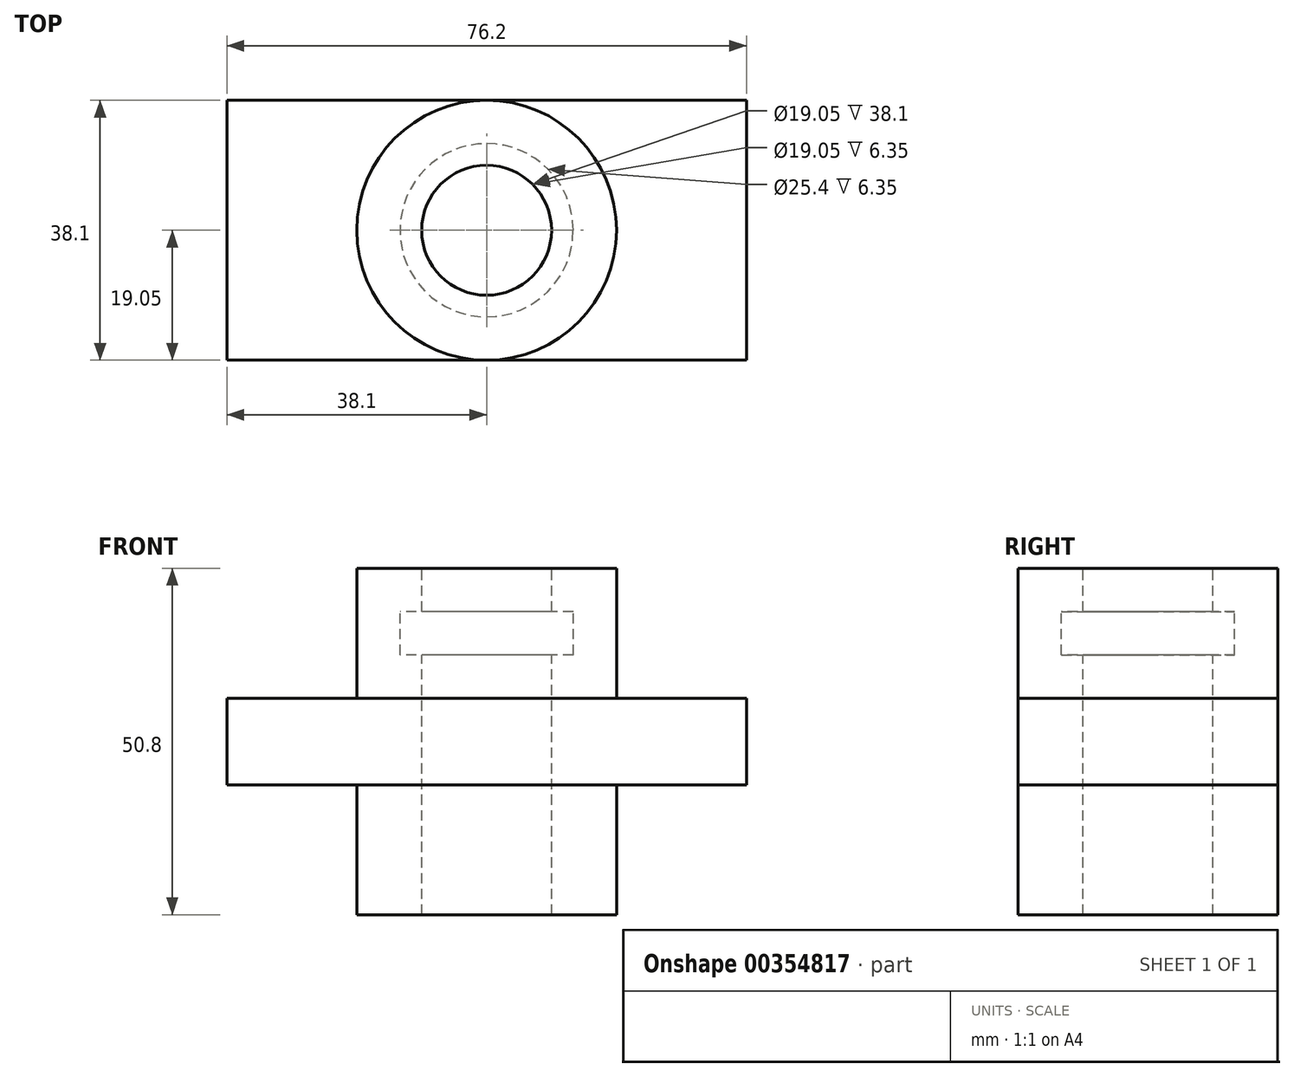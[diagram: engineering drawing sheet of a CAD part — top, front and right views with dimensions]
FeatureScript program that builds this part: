
annotation { "Feature Type Name" : "Feature", "Feature Type Description" : "" }
export const myFeature = defineFeature(function(context is Context, id is Id, definition is map)
    precondition{}
    {
        {
            var Q0;
            Q0=qCreatedBy(makeId("Top.planeOp"),FACE);
            var sketch = newSketch(context, id + "F0", { "sketchPlane" : qUnion([Q0])});
            skCircle(sketch, "E0", {"center": v(0, 0) * mm, "radius": 19.05 * mm});
            skLineSegment(sketch, "E1", {"start": v(0, 19.05) * mm, "end": v(38.1, 19.05) * mm});
            skLineSegment(sketch, "E2", {"start": v(0, -19.05) * mm, "end": v(38.1, -19.05) * mm});
            skLineSegment(sketch, "E3", {"start": v(38.1, 19.05) * mm, "end": v(38.1, -19.05) * mm});
            skLineSegment(sketch, "E4", {"start": v(0, 19.05) * mm, "end": v(-38.1, 19.05) * mm});
            skLineSegment(sketch, "E5", {"start": v(0, -19.05) * mm, "end": v(-38.1, -19.05) * mm});
            skLineSegment(sketch, "E6", {"start": v(-38.1, 19.05) * mm, "end": v(-38.1, -19.05) * mm});
            skSolve(sketch);
        }
        {
            var Q0;
            {var subQ0=sQuery(id+"F0.wireOp",EDGE,"E0");var subQ1=makeQuery(id+"F0.imprint","INTERSECT",VERTEX,{"derivedFrom":[subQ0,sQuery(id+"F0.wireOp",EDGE,"E1"),sQuery(id+"F0.wireOp",EDGE,"E4")]});Q0=makeQuery(id+"F0.imprint","IMPRINT",FACE,{"disambiguationData":[TD([[makeQuery(id+"F0.imprint","IMPRINT",EDGE,{"disambiguationData":[TD([[subQ1,-1.0]])],"derivedFrom":subQ0}),1.0]])]});}
            extrude(context, id + "F1", {"entities" : qUnion([Q0]), "endBound" : BoundingType.SYMMETRIC, "depth" : 50.8 * mm});
        }
        {
            var Q0;
            {var subQ0=sQuery(id+"F0.wireOp",EDGE,"E1");Q0=makeQuery(id+"F0.imprint","IMPRINT",FACE,{"disambiguationData":[TD([[makeQuery(id+"F0.imprint","IMPRINT",EDGE,{"derivedFrom":subQ0}),-1.0]])]});}
            var Q1;
            {var subQ0=sQuery(id+"F0.wireOp",EDGE,"E4");Q1=makeQuery(id+"F0.imprint","IMPRINT",FACE,{"disambiguationData":[TD([[makeQuery(id+"F0.imprint","IMPRINT",EDGE,{"derivedFrom":subQ0}),1.0]])]});}
            extrude(context, id + "F2", {"entities" : qUnion([Q0, Q1]), "operationType" : NewBodyOperationType.ADD, "endBound" : BoundingType.SYMMETRIC, "depth" : 12.7 * mm});
        }
        {
            var Q0;
            Q0=makeQuery(id+"F1.opExtrude","CAP_FACE",FACE,{"disambiguationData":[OSD([sQuery(id+"F0.wireOp",EDGE,"E0")])],"isStart":false});
            var sketch = newSketch(context, id + "F3", { "sketchPlane" : qUnion([Q0])});
            skCircle(sketch, "E7", {"center": v(0, 0) * mm, "radius": 9.53 * mm});
            skCircle(sketch, "E8", {"center": v(0, 0) * mm, "radius": 12.7 * mm});
            skSolve(sketch);
        }
        {
            var Q0;
            Q0=makeQuery(id+"F3.imprint","IMPRINT",FACE,{"disambiguationData":[TD([[makeQuery(id+"F3.imprint","IMPRINT",EDGE,{"derivedFrom":sQuery(id+"F3.wireOp",EDGE,"E7")}),1.0]])]});
            extrude(context, id + "F4", {"entities" : qUnion([Q0]), "operationType" : NewBodyOperationType.REMOVE, "endBound" : BoundingType.THROUGH_ALL, "oppositeDirection" : true, "depth" : 25.4 * mm});
        }
        {
            var Q0;
            Q0=makeQuery(id+"F3.imprint","IMPRINT",FACE,{"disambiguationData":[TD([[makeQuery(id+"F3.imprint","IMPRINT",EDGE,{"derivedFrom":sQuery(id+"F3.wireOp",EDGE,"E7")}),-1.0]])]});
            extrude(context, id + "F5", {"entities" : qUnion([Q0]), "operationType" : NewBodyOperationType.REMOVE, "oppositeDirection" : true, "depth" : 12.7 * mm, "hasSecondDirection" : true, "secondDirectionOppositeDirection" : true, "secondDirectionDepth" : 6.35 * mm});
        }
    });
